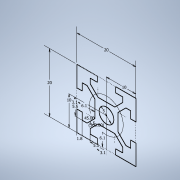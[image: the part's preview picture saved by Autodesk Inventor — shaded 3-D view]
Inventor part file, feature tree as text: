
AUTODESK INVENTOR PART (.ipt)
format: ipt  version: 2022 (Build 260153000, 153)  size: 167,424 bytes
history: native  units: mm
features: extrude x1, sketch x1
ambient origin geometry x8: Origin, YZ Plane, XZ Plane, XY Plane, X Axis, Y Axis, Z Axis, Center Point
bodies: Solid1 (feature_tree)
feature tree (2):
  extrude  "Extrusion1"  Depth=20.0mm
  sketch  "Sketch1"  dims[d0=20.0mm d1=20.0mm d2=10.0mm d3=10.0mm d4=3.1mm d5=5.5mm d6=5.5mm d7=3.1mm d8=1.8mm d10=6.1mm d11=6.1mm d12=45.0deg d13=1.5mm d14=40.0mm d16=360.0deg d18=5.0mm d19=710.0mm d20=0.0mm]
